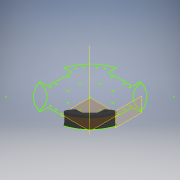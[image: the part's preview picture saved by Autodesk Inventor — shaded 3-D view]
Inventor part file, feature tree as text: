
AUTODESK INVENTOR PART (.ipt)
format: ipt  version: 2020 (Build 240168000, 168)  size: 180,224 bytes
history: native  units: mm
features: other x4, sketch x4, extrude x3, mirror x1
ambient origin geometry x8: Origin, YZ Plane, XZ Plane, XY Plane, X Axis, Y Axis, Z Axis, Center Point
bodies: Body1 (feature_tree)
feature tree (12):
  other  "Твердое тело1"
  sketch  "Эскиз1"
  extrude  "Выдавливание1"  Depth=4.0mm
  other  "РабПлоскость1"
  extrude  "Выдавливание2"  Depth=4.0mm
  other  "РабПлоскость2"
  extrude  "Выдавливание3"  Depth=8.0mm
  other  "РабПлоскость3"
  mirror  "Зеркальное отражение1"
  sketch  "Эскиз2"
  sketch  "Эскиз3"
  sketch  "Эскиз4"
